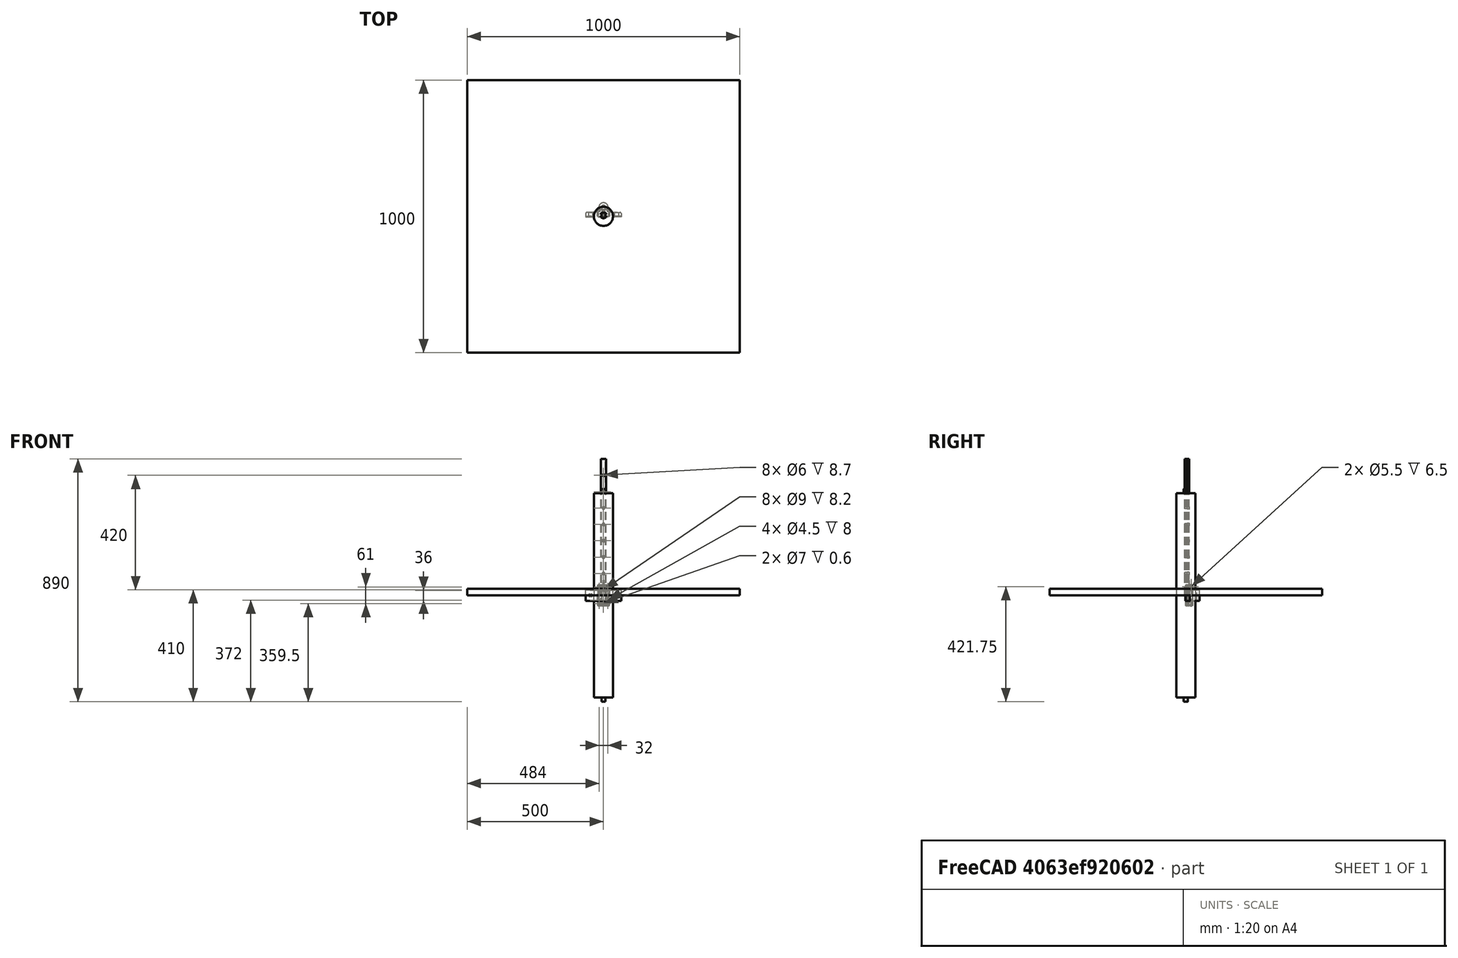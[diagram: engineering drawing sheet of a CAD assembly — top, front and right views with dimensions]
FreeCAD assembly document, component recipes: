
FREECAD ASSEMBLY — COMPONENT RECIPES ("Cutting")

This assembly document has 5 components, labeled P0..P4 below (a component is one placed body or linked part). 4 of them carry a construction recipe — the FreeCAD feature program that regenerates the part from scratch, quoted from this document or its linked companion documents; the rest are supplied as boundary geometry only. No exploded tour is included for this assembly.
COMPONENT P0 — geometry summary ("Model"; no construction recipe available for this part):
  bounding box: 130.0 x 40.0 x 2.0 mm
  tessellated surface: 32 triangles
  volume: 10400 mm^3 (100% of its bounding box)
  symmetry: 2-fold rotationally symmetric about the x axis; 2-fold rotationally symmetric about the y axis; 2-fold rotationally symmetric about the z axis; mirror-symmetric across its x mid-plane, y mid-plane, z mid-plane
COMPONENT P1 — recipe-attached ("bearing_holder", modeled in this document).
Construction recipe (the document's own serialized feature program — sketch geometry with constraints, then the solid features built on it; lengths are millimeters unless a unit is written):

FEATURE [Sketcher::SketchObject] Sketch
  FullyConstrained = true
  MapMode = 5
  Support = -> [XY_Plane]
  sketch-geometry (12):
    g0: ArcOfCircle CenterX=0 CenterY=33 CenterZ=0 NormalX=0 NormalY=0 NormalZ=1 AngleXU=0 Radius=7.5 StartAngle=4.71239 EndAngle=7.85398
    g1: ArcOfCircle CenterX=0 CenterY=33 CenterZ=0 NormalX=0 NormalY=0 NormalZ=1 AngleXU=0 Radius=17 StartAngle=0 EndAngle=1.5708
    g2: ArcOfCircle CenterX=35 CenterY=33 CenterZ=0 NormalX=0 NormalY=0 NormalZ=1 AngleXU=0 Radius=18 StartAngle=3.14159 EndAngle=4.71239
    g3: ArcOfCircle CenterX=60 CenterY=10 CenterZ=0 NormalX=0 NormalY=0 NormalZ=1 AngleXU=0 Radius=5 StartAngle=0 EndAngle=1.5708
    g4: LineSegment StartX=65 StartY=10 StartZ=0 EndX=65 EndY=0 EndZ=0
    g5: LineSegment StartX=65 StartY=0 StartZ=0 EndX=0 EndY=0 EndZ=0
    g6: LineSegment StartX=0 StartY=0 StartZ=0 EndX=6.981e-13 EndY=25.5 EndZ=0
    g7: LineSegment StartX=-1.6097e-12 StartY=40.5 StartZ=0 EndX=1e-15 EndY=50 EndZ=0
    g8: LineSegment StartX=47.5 StartY=0 StartZ=0 EndX=47.5 EndY=15 EndZ=0
    g9: LineSegment StartX=35 StartY=15 StartZ=0 EndX=47.5 EndY=15 EndZ=0
    g10: LineSegment StartX=47.5 StartY=15 StartZ=0 EndX=60 EndY=15 EndZ=0
    g11: LineSegment StartX=17 StartY=33 StartZ=0 EndX=17 EndY=0 EndZ=0
  constraints (33):
    c: PointOnObject(g0,g-2)
    c: PointOnObject(g0,g-2)
    c: PointOnObject(g0,g-2)
    c: Coincident(g1,g0)
    c: PointOnObject(g1,g-2)
    c: PointOnObject(g4,g-1)
    c: Vertical(g4)
    c: Coincident(g5,g4)
    c: Coincident(g5,g-1)
    c: Coincident(g6,g5)
    c: Coincident(g6,g0)
    c: Coincident(g7,g0)
    c: Coincident(g7,g1)
    c: DistanceX(g4) = 65  'width'
    c: PointOnObject(g8,g5)
    c: Vertical(g8)
    c: DistanceX(g8) = 47.5  'hole_distance'
    c: DistanceY(g0) = 33  'hole_height'
    c: Tangent(g9,g2) = -1.5708
    c: Tangent(g2,g1) = 1.5708
    c: Distance(g8) = 15
    c: Tangent(g10,g3) = 1.5708
    c: Tangent(g4,g3) = 1.5708
    c: Coincident(g9,g10)
    c: Horizontal(g9)
    c: Horizontal(g10)
    c: Coincident(g9,g8)
    c: Equal(g9,g10)
    c: DistanceX(g2,g3) = 25
    c: Diameter(g0) = 15  'hole_d'
    c: PointOnObject(g11,g-1)
    c: Vertical(g11)
    c: Tangent(g11,g1) = 1.5708
FEATURE [PartDesign::Pad] Pad
  Direction = (0,0,1)
  Length = 40
  Length2 = 10
  Midplane = true
  Profile = -> Sketch
  ReferenceAxis = -> Sketch [N_Axis]
  Type = 0
FEATURE [Sketcher::SketchObject] Sketch001
  FullyConstrained = true
  MapMode = 5
  Placement = pos=(0,0,0) rot=(1,0,0;1.5708rad)
  Support = -> [XZ_Plane]
  sketch-geometry (8):
    g0: ArcOfCircle CenterX=50 CenterY=0 CenterZ=0 NormalX=0 NormalY=0 NormalZ=1 AngleXU=0 Radius=5 StartAngle=4.71239 EndAngle=7.85398
    g1: ArcOfCircle CenterX=45 CenterY=0 CenterZ=0 NormalX=0 NormalY=0 NormalZ=1 AngleXU=0 Radius=5 StartAngle=1.5708 EndAngle=4.71239
    g2: LineSegment StartX=50 StartY=5 StartZ=0 EndX=45 EndY=5 EndZ=0
    g3: LineSegment StartX=45 StartY=-5 StartZ=0 EndX=50 EndY=-5 EndZ=0
    g4: GeomPoint X=40 Y=0 Z=0
    g5: GeomPoint X=55 Y=0 Z=0
    g6: LineSegment StartX=45 StartY=0 StartZ=0 EndX=47.5 EndY=0 EndZ=0
    g7: LineSegment StartX=47.5 StartY=0 StartZ=0 EndX=50 EndY=0 EndZ=0
  constraints (19):
    c: Tangent(g0,g2) = -1.5708
    c: Tangent(g2,g1) = -1.5708
    c: Tangent(g1,g3) = -1.5708
    c: Tangent(g3,g0) = -1.5708
    c: Equal(g0,g1)
    c: PointOnObject(g0,g-1)
    c: PointOnObject(g1,g-1)
    c: PointOnObject(g4,g1)
    c: PointOnObject(g5,g0)
    c: PointOnObject(g5,g-1)
    c: PointOnObject(g4,g-1)
    c: DistanceX(g4,g5) = 15
    c: DistanceY(g0,g0) = 10
    c: Coincident(g6,g1)
    c: Horizontal(g6)
    c: Coincident(g7,g6)
    c: Coincident(g7,g0)
    c: Equal(g6,g7)
    c: DistanceX(g6) = 47.5
FEATURE [PartDesign::Pocket] Pocket
  BaseFeature = -> Pad
  Direction = (0,1,2e-16)
  Length = 5
  Length2 = 5
  Profile = -> Sketch001
  ReferenceAxis = -> Sketch001 [N_Axis]
  Type = 1
FEATURE [PartDesign::Mirrored] Mirrored
  BaseFeature = -> Pocket
  MirrorPlane = -> Sketch [V_Axis]
  Originals = -> [Pad,Pocket]
FEATURE [PartDesign::Body] Body
  Group = -> [Sketch,Pad,Sketch001,Pocket,Mirrored]
  Origin = -> Origin
  Tip = -> Mirrored
COMPONENT P2 — recipe-attached ("roll", modeled in this document).
Construction recipe (the document's own serialized feature program — sketch geometry with constraints, then the solid features built on it; lengths are millimeters unless a unit is written):

FEATURE [PartDesign::AdditiveCylinder] Cylinder
  Angle = 360
  AttacherType = Attacher::AttachEngine3D
  FirstAngle = 0
  Height = 375
  Radius = 35
  SecondAngle = 0
FEATURE [PartDesign::AdditiveCylinder] Cylinder001
  Angle = 360
  AttacherType = Attacher::AttachEngine3D
  BaseFeature = -> Cylinder
  FirstAngle = 0
  Height = 390
  MapMode = 5
  Radius = 7.5
  SecondAngle = 0
  Support = -> [XY_Plane001]
FEATURE [PartDesign::Mirrored] Mirrored001
  BaseFeature = -> Cylinder001
  MirrorPlane = -> XY_Plane001
  Originals = -> [Cylinder,Cylinder001]
FEATURE [PartDesign::Body] Body001
  Group = -> [Cylinder,Cylinder001,Mirrored001]
  Origin = -> Origin001
  Tip = -> Mirrored001
COMPONENT P3 — recipe-attached ("insertion", modeled in this document).
Construction recipe (the document's own serialized feature program — sketch geometry with constraints, then the solid features built on it; lengths are millimeters unless a unit is written):

FEATURE [Sketcher::SketchObject] Sketch002
  FullyConstrained = true
  MapMode = 5
  Placement = pos=(0,0,0) rot=(1,0,0;1.5708rad)
  Support = -> [XZ_Plane002]
  expr: Constraints[10] = Sketch.Constraints.width
  expr: Constraints[9] = Pad.Length / 2
  sketch-geometry (4):
    g0: LineSegment StartX=0 StartY=0 StartZ=0 EndX=65 EndY=0 EndZ=0
    g1: LineSegment StartX=65 StartY=0 StartZ=0 EndX=65 EndY=20 EndZ=0
    g2: LineSegment StartX=65 StartY=20 StartZ=0 EndX=0 EndY=20 EndZ=0
    g3: LineSegment StartX=0 StartY=20 StartZ=0 EndX=0 EndY=0 EndZ=0
  constraints (11):
    c: Coincident(g0,g1)
    c: Coincident(g1,g2)
    c: Coincident(g2,g3)
    c: Coincident(g3,g0)
    c: Horizontal(g0)
    c: Horizontal(g2)
    c: Vertical(g1)
    c: Vertical(g3)
    c: Coincident(g0,g-1)
    c: DistanceY(g3,g3) = 20
    c: DistanceX(g0,g0) = 65
FEATURE [PartDesign::Pad] Pad001
  Direction = (0,-1,-2e-16)
  Length = 2
  Length2 = 10
  Placement = pos=(0,0,0) rot=(1,0,0;1.5708rad)
  Profile = -> Sketch002
  ReferenceAxis = -> Sketch002 [N_Axis]
  Type = 0
FEATURE [PartDesign::Mirrored] Mirrored002
  MirrorPlane = -> Sketch002 [V_Axis]
  Placement = pos=(0,0,0) rot=(1,0,0;1.5708rad)
FEATURE [PartDesign::Mirrored] Mirrored003
  MirrorPlane = -> Sketch002 [H_Axis]
  Placement = pos=(0,0,0) rot=(1,0,0;1.5708rad)
FEATURE [PartDesign::MultiTransform] MultiTransform
  BaseFeature = -> Pad001
  Originals = -> [Pad001]
  Placement = pos=(0,0,0) rot=(1,0,0;1.5708rad)
  Transformations = -> [Mirrored002,Mirrored003]
FEATURE [PartDesign::Body] Body002
  Group = -> [Sketch002,Pad001,MultiTransform,Mirrored002,Mirrored003]
  Origin = -> Origin002
  Tip = -> MultiTransform
COMPONENT P4 — recipe-attached ("plywood", modeled in this document).
Construction recipe (the document's own serialized feature program — sketch geometry with constraints, then the solid features built on it; lengths are millimeters unless a unit is written):

FEATURE [Sketcher::SketchObject] Sketch003
  FullyConstrained = true
  MapMode = 5
  Support = -> [XY_Plane003]
  sketch-geometry (5):
    g0: LineSegment StartX=-500 StartY=-500 StartZ=0 EndX=-500 EndY=500 EndZ=0
    g1: LineSegment StartX=-500 StartY=500 StartZ=0 EndX=500 EndY=500 EndZ=0
    g2: LineSegment StartX=500 StartY=500 StartZ=0 EndX=500 EndY=-500 EndZ=0
    g3: LineSegment StartX=500 StartY=-500 StartZ=0 EndX=-500 EndY=-500 EndZ=0
    g4: GeomPoint X=0 Y=2.5e-15 Z=0
  constraints (12):
    c: Coincident(g0,g1)
    c: Coincident(g1,g2)
    c: Coincident(g2,g3)
    c: Coincident(g3,g0)
    c: Horizontal(g1)
    c: Horizontal(g3)
    c: Vertical(g0)
    c: Vertical(g2)
    c: Symmetric(g1,g0,g4)
    c: Coincident(g4,g-1)
    c: Equal(g2,g1)
    c: Distance(g1) = 1000
FEATURE [PartDesign::Pad] Pad002
  Direction = (0,0,1)
  Length = 24
  Length2 = 10
  Profile = -> Sketch003
  ReferenceAxis = -> Sketch003 [N_Axis]
  Type = 0
FEATURE [PartDesign::Body] Body003
  Group = -> [Sketch003,Pad002]
  Origin = -> Origin003
  Tip = -> Pad002
PROVENANCE & LICENSES
A FreeCAD (.FCStd) document from a public repository crawl; recipes are the document's own serialized feature recipes (and, for linked parts, companion documents' recipes).
License: as declared in the source repository (recorded in the dataset sidecar).
